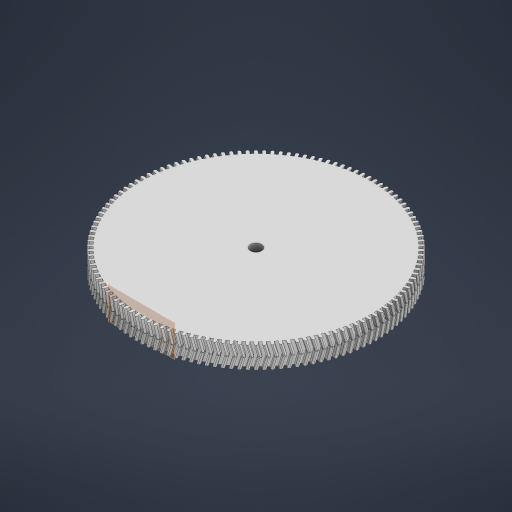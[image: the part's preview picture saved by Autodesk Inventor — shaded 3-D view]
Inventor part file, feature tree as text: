
AUTODESK INVENTOR PART (.ipt)
format: ipt  version: 2023 (Build 270158030, 158C)  size: 1,997,824 bytes
history: native  units: in
note: dims shown in document units (in); Inventor stores cm internally (conversion verified against a paired STEP export)
features: extrude x4, sketch x4, plane x1, fillet x1, pattern_circular x1
ambient origin geometry x8: Origin, YZ Plane, XZ Plane, XY Plane, X Axis, Y Axis, Z Axis, Center Point
bodies: Solid1 (feature_tree)
feature tree (11):
  extrude  "Extrusion1"  Depth=0.5906in TaperAngle=0.0deg
  plane  "Work Plane1"
  extrude  "Extrusion2"  Depth=3.1299in
  extrude  "Extrusion5"  Depth=0.0787in
  fillet  "Fillet2"  Radius=0.1378in
  pattern_circular  "Circular Pattern3"  [2 undecoded]
  extrude  "Extrusion7"  Depth=0.0394in
  sketch  "Sketch3"  dims[d0=6.2992in d1=0.5906in d2=0.0in]
  sketch  "Sketch8"  dims[d3=3.1299in d4=0.0787in]
  sketch  "Sketch14"  dims[d5=0.0787in d6=0.0787in d7=0.1378in d8=0.0in]
  sketch  "Sketch17"  dims[d24=0.3071in d25=0.5906in d26=0.0in d40=0.0394in d41=49.4739in d42=360.0deg d44=1.1811in d45=0.0in d43=0.0in d46=0.0197in d47=0.0344in]
note: 2 required parameter values undecoded (feature->parameter linkage not recoverable at this tier; creation-order binding heuristic only, values carry confidence <= 0.55)
